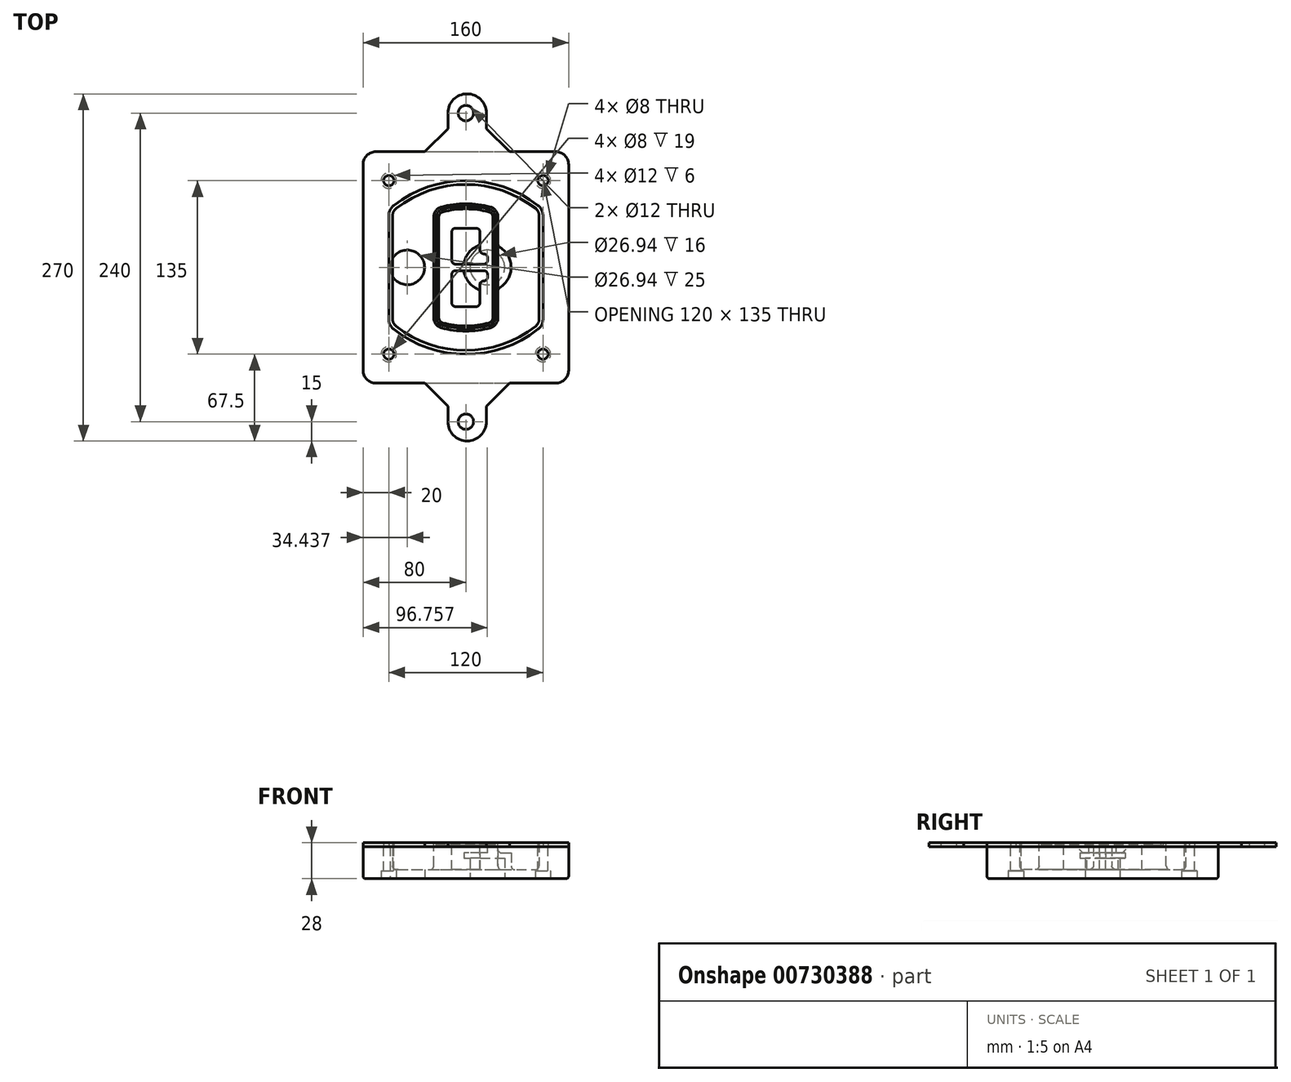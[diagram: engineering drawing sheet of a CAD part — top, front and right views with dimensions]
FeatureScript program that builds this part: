
annotation { "Feature Type Name" : "Feature", "Feature Type Description" : "" }
export const myFeature = defineFeature(function(context is Context, id is Id, definition is map)
    precondition{}
    {
        {
            var Q0;
            Q0=qCreatedBy(makeId("Top.planeOp"),FACE);
            var sketch = newSketch(context, id + "F0", { "sketchPlane" : qUnion([Q0])});
            skPoint(sketch, "E0.rect.middle", {"position": v(0, 0) * mm});
            skLineSegment(sketch, "E1.bottom", {"start": v(-70, -90) * mm, "end": v(70, -90) * mm});
            skLineSegment(sketch, "E1.top", {"start": v(-70, 90) * mm, "end": v(70, 90) * mm});
            skLineSegment(sketch, "E1.left", {"start": v(-80, -80) * mm, "end": v(-80, 80) * mm});
            skLineSegment(sketch, "E1.right", {"start": v(80, -80) * mm, "end": v(80, 80) * mm});
            skLineSegment(sketch, "E2", {"start": v(-80, 90) * mm, "end": v(80, -90) * mm, "construction": true});
            skLineSegment(sketch, "E3", {"start": v(80, 90) * mm, "end": v(-80, -90) * mm, "construction": true});
            skCircle(sketch, "E4", {"center": v(-60, 67.5) * mm, "radius": 4 * mm});
            skCircle(sketch, "E5", {"center": v(60, 67.5) * mm, "radius": 4 * mm});
            skCircle(sketch, "E6", {"center": v(60, -67.5) * mm, "radius": 4 * mm});
            skCircle(sketch, "E7", {"center": v(-60, -67.5) * mm, "radius": 4 * mm});
            skLineSegment(sketch, "E8", {"start": v(-60, 67.5) * mm, "end": v(60, 67.5) * mm, "construction": true});
            skLineSegment(sketch, "E9", {"start": v(60, 67.5) * mm, "end": v(60, -67.5) * mm, "construction": true});
            skLineSegment(sketch, "E10", {"start": v(60, -67.5) * mm, "end": v(-60, -67.5) * mm, "construction": true});
            skLineSegment(sketch, "E11", {"start": v(-60, -67.5) * mm, "end": v(-60, 67.5) * mm, "construction": true});
            skLineSegment(sketch, "E12", {"start": v(-60, 40.3) * mm, "end": v(-60, -40.3) * mm});
            skLineSegment(sketch, "E13", {"start": v(60, 40.3) * mm, "end": v(60, -40.3) * mm});
            skArc(sketch, "E14", {"start": v(56.15, 48.18) * mm, "mid": v(0, 67.5) * mm, "end": v(-56.15, 48.18) * mm});
            skArc(sketch, "E15", {"start": v(-56.15, -48.18) * mm, "mid": v(0, -67.5) * mm, "end": v(56.15, -48.18) * mm});
            skLineSegment(sketch, "E16", {"start": v(-60, 0) * mm, "end": v(60, 0) * mm, "construction": true});
            skPoint(sketch, "E17.visualSharp", {"position": v(-60, -45) * mm});
            skArc(sketch, "E17.filletArc", {"start": v(-60, -40.3) * mm, "mid": v(-58.99, -44.68) * mm, "end": v(-56.15, -48.18) * mm});
            skPoint(sketch, "E18.visualSharp", {"position": v(-60, 45) * mm});
            skArc(sketch, "E18.filletArc", {"start": v(-56.15, 48.18) * mm, "mid": v(-58.99, 44.68) * mm, "end": v(-60, 40.3) * mm});
            skPoint(sketch, "E19.visualSharp", {"position": v(60, 45) * mm});
            skArc(sketch, "E19.filletArc", {"start": v(60, 40.3) * mm, "mid": v(58.99, 44.68) * mm, "end": v(56.15, 48.18) * mm});
            skPoint(sketch, "E20.visualSharp", {"position": v(60, -45) * mm});
            skArc(sketch, "E20.filletArc", {"start": v(56.15, -48.18) * mm, "mid": v(58.99, -44.68) * mm, "end": v(60, -40.3) * mm});
            skPoint(sketch, "E21.visualSharp", {"position": v(-80, 90) * mm});
            skArc(sketch, "E21.filletArc", {"start": v(-70, 90) * mm, "mid": v(-77.07, 87.07) * mm, "end": v(-80, 80) * mm});
            skPoint(sketch, "E22.visualSharp", {"position": v(80, 90) * mm});
            skArc(sketch, "E22.filletArc", {"start": v(80, 80) * mm, "mid": v(77.07, 87.07) * mm, "end": v(70, 90) * mm});
            skPoint(sketch, "E23.visualSharp", {"position": v(80, -90) * mm});
            skArc(sketch, "E23.filletArc", {"start": v(70, -90) * mm, "mid": v(77.07, -87.07) * mm, "end": v(80, -80) * mm});
            skPoint(sketch, "E24.visualSharp", {"position": v(-80, -90) * mm});
            skArc(sketch, "E24.filletArc", {"start": v(-80, -80) * mm, "mid": v(-77.07, -87.07) * mm, "end": v(-70, -90) * mm});
            skArc(sketch, "E25.0", {"start": v(57, 40.3) * mm, "mid": v(56.3, 43.36) * mm, "end": v(54.3, 45.81) * mm});
            skLineSegment(sketch, "E25.1", {"start": v(57, 40.3) * mm, "end": v(57, -40.3) * mm});
            skArc(sketch, "E25.2", {"start": v(54.3, -45.81) * mm, "mid": v(56.3, -43.36) * mm, "end": v(57, -40.3) * mm});
            skArc(sketch, "E25.3", {"start": v(-54.3, -45.81) * mm, "mid": v(0, -64.5) * mm, "end": v(54.3, -45.81) * mm});
            skArc(sketch, "E25.4", {"start": v(-57, -40.3) * mm, "mid": v(-56.3, -43.36) * mm, "end": v(-54.3, -45.81) * mm});
            skArc(sketch, "E25.5", {"start": v(54.3, 45.81) * mm, "mid": v(0, 64.5) * mm, "end": v(-54.3, 45.81) * mm});
            skLineSegment(sketch, "E25.6", {"start": v(-57, 40.3) * mm, "end": v(-57, -40.3) * mm});
            skArc(sketch, "E25.7", {"start": v(-54.3, 45.81) * mm, "mid": v(-56.3, 43.36) * mm, "end": v(-57, 40.3) * mm});
            skArc(sketch, "E26.0", {"start": v(-58.62, 51.33) * mm, "mid": v(-62.58, 46.43) * mm, "end": v(-64, 40.3) * mm});
            skArc(sketch, "E26.1", {"start": v(58.62, 51.33) * mm, "mid": v(0, 71.5) * mm, "end": v(-58.62, 51.33) * mm});
            skArc(sketch, "E26.2", {"start": v(64, 40.3) * mm, "mid": v(62.58, 46.43) * mm, "end": v(58.62, 51.33) * mm});
            skLineSegment(sketch, "E26.3", {"start": v(64, 40.3) * mm, "end": v(64, -40.3) * mm});
            skArc(sketch, "E26.4", {"start": v(58.62, -51.33) * mm, "mid": v(62.58, -46.43) * mm, "end": v(64, -40.3) * mm});
            skLineSegment(sketch, "E26.5", {"start": v(-64, 40.3) * mm, "end": v(-64, -40.3) * mm});
            skArc(sketch, "E26.6", {"start": v(-58.62, -51.33) * mm, "mid": v(0, -71.5) * mm, "end": v(58.62, -51.33) * mm});
            skArc(sketch, "E26.7", {"start": v(-64, -40.3) * mm, "mid": v(-62.58, -46.43) * mm, "end": v(-58.62, -51.33) * mm});
            skSolve(sketch);
        }
        {
            var Q0;
            Q0=makeQuery(id+"F0.imprint","IMPRINT",FACE,{"disambiguationData":[TD([[makeQuery(id+"F0.imprint","IMPRINT",EDGE,{"derivedFrom":sQuery(id+"F0.wireOp",EDGE,"E1.bottom")}),1.0]])]});
            var Q1;
            Q1=makeQuery(id+"F0.imprint","IMPRINT",FACE,{"disambiguationData":[TD([[makeQuery(id+"F0.imprint","IMPRINT",EDGE,{"derivedFrom":sQuery(id+"F0.wireOp",EDGE,"E12")}),1.0]])]});
            var Q2;
            Q2=makeQuery(id+"F0.imprint","IMPRINT",FACE,{"disambiguationData":[TD([[makeQuery(id+"F0.imprint","IMPRINT",EDGE,{"derivedFrom":sQuery(id+"F0.wireOp",EDGE,"E25.0")}),1.0]])]});
            var Q3;
            Q3=makeQuery(id+"F0.imprint","IMPRINT",FACE,{"disambiguationData":[TD([[makeQuery(id+"F0.imprint","IMPRINT",EDGE,{"derivedFrom":sQuery(id+"F0.wireOp",EDGE,"E12")}),-1.0]])]});
            extrude(context, id + "F1", {"entities" : qUnion([Q0, Q1, Q2, Q3]), "oppositeDirection" : true, "depth" : 25 * mm});
        }
        {
            var Q0;
            Q0=makeQuery(id+"F0.imprint","IMPRINT",FACE,{"disambiguationData":[TD([[makeQuery(id+"F0.imprint","IMPRINT",EDGE,{"derivedFrom":sQuery(id+"F0.wireOp",EDGE,"E12")}),1.0]])]});
            extrude(context, id + "F2", {"entities" : qUnion([Q0]), "operationType" : NewBodyOperationType.ADD, "depth" : 3 * mm});
        }
        {
            var Q0;
            Q0=makeQuery(id+"F0.imprint","IMPRINT",FACE,{"disambiguationData":[TD([[makeQuery(id+"F0.imprint","IMPRINT",EDGE,{"derivedFrom":sQuery(id+"F0.wireOp",EDGE,"E25.0")}),1.0]])]});
            extrude(context, id + "F3", {"entities" : qUnion([Q0]), "operationType" : NewBodyOperationType.REMOVE, "oppositeDirection" : true, "depth" : 18 * mm});
        }
        {
            var Q0;
            Q0=makeQuery(id+"F2.opExtrude","CAP_FACE",FACE,{"disambiguationData":[OSD([sQuery(id+"F0.wireOp",EDGE,"E12"),sQuery(id+"F0.wireOp",EDGE,"E13"),sQuery(id+"F0.wireOp",EDGE,"E14"),sQuery(id+"F0.wireOp",EDGE,"E15"),sQuery(id+"F0.wireOp",EDGE,"E17.filletArc"),sQuery(id+"F0.wireOp",EDGE,"E18.filletArc"),sQuery(id+"F0.wireOp",EDGE,"E19.filletArc"),sQuery(id+"F0.wireOp",EDGE,"E20.filletArc"),sQuery(id+"F0.wireOp",EDGE,"E25.0"),sQuery(id+"F0.wireOp",EDGE,"E25.1"),sQuery(id+"F0.wireOp",EDGE,"E25.2"),sQuery(id+"F0.wireOp",EDGE,"E25.3"),sQuery(id+"F0.wireOp",EDGE,"E25.4"),sQuery(id+"F0.wireOp",EDGE,"E25.5"),sQuery(id+"F0.wireOp",EDGE,"E25.6"),sQuery(id+"F0.wireOp",EDGE,"E25.7")])],"isStart":false});
            var sketch = newSketch(context, id + "F4", { "sketchPlane" : qUnion([Q0])});
            skArc(sketch, "E27.0", {"start": v(-19.08, -46.97) * mm, "mid": v(0, -49.5) * mm, "end": v(19.08, -46.97) * mm});
            skArc(sketch, "E28.0", {"start": v(19.08, 46.97) * mm, "mid": v(0, 49.5) * mm, "end": v(-19.08, 46.97) * mm});
            skLineSegment(sketch, "E29", {"start": v(-25, 39.25) * mm, "end": v(-25, -39.25) * mm});
            skLineSegment(sketch, "E30", {"start": v(25, 39.25) * mm, "end": v(25, -39.25) * mm});
            skLineSegment(sketch, "E31", {"start": v(-25, 45.1) * mm, "end": v(25, 45.1) * mm, "construction": true});
            skLineSegment(sketch, "E32", {"start": v(-25, -45.1) * mm, "end": v(25, -45.1) * mm, "construction": true});
            skPoint(sketch, "E33.visualSharp", {"position": v(-25, 45.1) * mm});
            skArc(sketch, "E33.filletArc", {"start": v(-19.08, 46.97) * mm, "mid": v(-23.35, 44.11) * mm, "end": v(-25, 39.25) * mm});
            skPoint(sketch, "E34.visualSharp", {"position": v(25, 45.1) * mm});
            skArc(sketch, "E34.filletArc", {"start": v(25, 39.25) * mm, "mid": v(23.35, 44.11) * mm, "end": v(19.08, 46.97) * mm});
            skPoint(sketch, "E35.visualSharp", {"position": v(25, -45.1) * mm});
            skArc(sketch, "E35.filletArc", {"start": v(19.08, -46.97) * mm, "mid": v(23.35, -44.11) * mm, "end": v(25, -39.25) * mm});
            skPoint(sketch, "E36.visualSharp", {"position": v(-25, -45.1) * mm});
            skArc(sketch, "E36.filletArc", {"start": v(-25, -39.25) * mm, "mid": v(-23.35, -44.11) * mm, "end": v(-19.08, -46.97) * mm});
            skArc(sketch, "E37.0", {"start": v(54.3, 45.81) * mm, "mid": v(0, 64.5) * mm, "end": v(-54.3, 45.81) * mm});
            skArc(sketch, "E37.1", {"start": v(-54.3, 45.81) * mm, "mid": v(-56.3, 43.36) * mm, "end": v(-57, 40.3) * mm});
            skLineSegment(sketch, "E37.2", {"start": v(-57, 40.3) * mm, "end": v(-57, -40.3) * mm});
            skArc(sketch, "E37.3", {"start": v(-57, -40.3) * mm, "mid": v(-56.3, -43.36) * mm, "end": v(-54.3, -45.81) * mm});
            skArc(sketch, "E37.4", {"start": v(-54.3, -45.81) * mm, "mid": v(0, -64.5) * mm, "end": v(54.3, -45.81) * mm});
            skArc(sketch, "E37.5", {"start": v(54.3, -45.81) * mm, "mid": v(56.3, -43.36) * mm, "end": v(57, -40.3) * mm});
            skLineSegment(sketch, "E37.6", {"start": v(57, 40.3) * mm, "end": v(57, -40.3) * mm});
            skArc(sketch, "E37.7", {"start": v(57, 40.3) * mm, "mid": v(56.3, 43.36) * mm, "end": v(54.3, 45.81) * mm});
            skLineSegment(sketch, "E38.0", {"start": v(23, 39.25) * mm, "end": v(23, -39.25) * mm});
            skArc(sketch, "E38.1", {"start": v(18.56, -45.04) * mm, "mid": v(21.76, -42.9) * mm, "end": v(23, -39.25) * mm});
            skArc(sketch, "E38.2", {"start": v(-18.56, -45.04) * mm, "mid": v(0, -47.5) * mm, "end": v(18.56, -45.04) * mm});
            skArc(sketch, "E38.3", {"start": v(-23, -39.25) * mm, "mid": v(-21.76, -42.9) * mm, "end": v(-18.56, -45.04) * mm});
            skLineSegment(sketch, "E38.4", {"start": v(-23, 39.25) * mm, "end": v(-23, -39.25) * mm});
            skArc(sketch, "E38.5", {"start": v(23, 39.25) * mm, "mid": v(21.76, 42.9) * mm, "end": v(18.56, 45.04) * mm});
            skArc(sketch, "E38.6", {"start": v(-18.56, 45.04) * mm, "mid": v(-21.76, 42.9) * mm, "end": v(-23, 39.25) * mm});
            skArc(sketch, "E38.7", {"start": v(18.56, 45.04) * mm, "mid": v(0, 47.5) * mm, "end": v(-18.56, 45.04) * mm});
            skArc(sketch, "E39.0", {"start": v(21, 39.25) * mm, "mid": v(20.18, 41.68) * mm, "end": v(18.04, 43.1) * mm});
            skLineSegment(sketch, "E39.1", {"start": v(21, 39.25) * mm, "end": v(21, -39.25) * mm});
            skArc(sketch, "E39.2", {"start": v(18.04, -43.1) * mm, "mid": v(20.18, -41.68) * mm, "end": v(21, -39.25) * mm});
            skArc(sketch, "E39.3", {"start": v(-18.04, -43.1) * mm, "mid": v(0, -45.5) * mm, "end": v(18.04, -43.1) * mm});
            skArc(sketch, "E39.4", {"start": v(-21, -39.25) * mm, "mid": v(-20.18, -41.68) * mm, "end": v(-18.04, -43.1) * mm});
            skArc(sketch, "E39.5", {"start": v(18.04, 43.1) * mm, "mid": v(0, 45.5) * mm, "end": v(-18.04, 43.1) * mm});
            skLineSegment(sketch, "E39.6", {"start": v(-21, 39.25) * mm, "end": v(-21, -39.25) * mm});
            skArc(sketch, "E39.7", {"start": v(-18.04, 43.1) * mm, "mid": v(-20.18, 41.68) * mm, "end": v(-21, 39.25) * mm});
            skLineSegment(sketch, "E40", {"start": v(-25, 0) * mm, "end": v(25, 0) * mm, "construction": true});
            skLineSegment(sketch, "E41", {"start": v(-11, 5.5) * mm, "end": v(-11, 27.5) * mm});
            skLineSegment(sketch, "E42", {"start": v(-8, 30.5) * mm, "end": v(8, 30.5) * mm});
            skLineSegment(sketch, "E43", {"start": v(11, 27.5) * mm, "end": v(11, 13.5) * mm});
            skLineSegment(sketch, "E44", {"start": v(14, 10.5) * mm, "end": v(14, 10.5) * mm});
            skLineSegment(sketch, "E45", {"start": v(17, 7.5) * mm, "end": v(17, 5.5) * mm});
            skLineSegment(sketch, "E46", {"start": v(14, 2.5) * mm, "end": v(-8, 2.5) * mm});
            skPoint(sketch, "E47.visualSharp", {"position": v(-11, 30.5) * mm});
            skArc(sketch, "E47.filletArc", {"start": v(-8, 30.5) * mm, "mid": v(-10.12, 29.62) * mm, "end": v(-11, 27.5) * mm});
            skPoint(sketch, "E48.visualSharp", {"position": v(11, 30.5) * mm});
            skArc(sketch, "E48.filletArc", {"start": v(11, 27.5) * mm, "mid": v(10.12, 29.62) * mm, "end": v(8, 30.5) * mm});
            skPoint(sketch, "E49.visualSharp", {"position": v(11, 10.5) * mm});
            skArc(sketch, "E49.filletArc", {"start": v(11, 13.5) * mm, "mid": v(11.88, 11.38) * mm, "end": v(14, 10.5) * mm});
            skPoint(sketch, "E50.visualSharp", {"position": v(17, 10.5) * mm});
            skArc(sketch, "E50.filletArc", {"start": v(17, 7.5) * mm, "mid": v(16.12, 9.62) * mm, "end": v(14, 10.5) * mm});
            skPoint(sketch, "E51.visualSharp", {"position": v(17, 2.5) * mm});
            skArc(sketch, "E51.filletArc", {"start": v(14, 2.5) * mm, "mid": v(16.12, 3.38) * mm, "end": v(17, 5.5) * mm});
            skPoint(sketch, "E52.visualSharp", {"position": v(-11, 2.5) * mm});
            skArc(sketch, "E52.filletArc", {"start": v(-11, 5.5) * mm, "mid": v(-10.12, 3.38) * mm, "end": v(-8, 2.5) * mm});
            skLineSegment(sketch, "E53.0.MirrorCS", {"start": v(14, -2.5) * mm, "end": v(-8, -2.5) * mm});
            skArc(sketch, "E54.0.MirrorCS", {"start": v(-11, -5.5) * mm, "mid": v(-10.12, -3.38) * mm, "end": v(-8, -2.5) * mm});
            skLineSegment(sketch, "E55.0.MirrorCS", {"start": v(-11, -5.5) * mm, "end": v(-11, -27.5) * mm});
            skArc(sketch, "E56.0.MirrorCS", {"start": v(-8, -30.5) * mm, "mid": v(-10.12, -29.62) * mm, "end": v(-11, -27.5) * mm});
            skLineSegment(sketch, "E57.0.MirrorCS", {"start": v(-8, -30.5) * mm, "end": v(8, -30.5) * mm});
            skArc(sketch, "E58.0.MirrorCS", {"start": v(11, -27.5) * mm, "mid": v(10.12, -29.62) * mm, "end": v(8, -30.5) * mm});
            skLineSegment(sketch, "E59.0.MirrorCS", {"start": v(11, -27.5) * mm, "end": v(11, -13.5) * mm});
            skArc(sketch, "E60.0.MirrorCS", {"start": v(11, -13.5) * mm, "mid": v(11.88, -11.38) * mm, "end": v(14, -10.5) * mm});
            skArc(sketch, "E61.0.MirrorCS", {"start": v(17, -7.5) * mm, "mid": v(16.12, -9.62) * mm, "end": v(14, -10.5) * mm});
            skLineSegment(sketch, "E62.0.MirrorCS", {"start": v(17, -7.5) * mm, "end": v(17, -5.5) * mm});
            skArc(sketch, "E63.0.MirrorCS", {"start": v(14, -2.5) * mm, "mid": v(16.12, -3.38) * mm, "end": v(17, -5.5) * mm});
            skSolve(sketch);
        }
        {
            var Q0;
            Q0=makeQuery(id+"F4.imprint","IMPRINT",FACE,{"disambiguationData":[TD([[makeQuery(id+"F4.imprint","IMPRINT",EDGE,{"derivedFrom":sQuery(id+"F4.wireOp",EDGE,"E27.0")}),1.0]])]});
            var Q1;
            Q1=makeQuery(id+"F4.imprint","IMPRINT",FACE,{"disambiguationData":[TD([[makeQuery(id+"F4.imprint","IMPRINT",EDGE,{"derivedFrom":sQuery(id+"F4.wireOp",EDGE,"E38.0")}),-1.0]])]});
            var Q2;
            Q2=makeQuery(id+"F4.imprint","IMPRINT",FACE,{"disambiguationData":[TD([[makeQuery(id+"F4.imprint","IMPRINT",EDGE,{"derivedFrom":sQuery(id+"F4.wireOp",EDGE,"E39.0")}),1.0]])]});
            extrude(context, id + "F5", {"entities" : qUnion([Q0, Q1, Q2]), "operationType" : NewBodyOperationType.ADD, "endBound" : BoundingType.UP_TO_NEXT, "oppositeDirection" : true, "depth" : 25 * mm});
        }
        {
            var Q0;
            Q0=makeQuery(id+"F4.imprint","IMPRINT",FACE,{"disambiguationData":[TD([[makeQuery(id+"F4.imprint","IMPRINT",EDGE,{"derivedFrom":sQuery(id+"F4.wireOp",EDGE,"E38.0")}),-1.0]])]});
            extrude(context, id + "F6", {"entities" : qUnion([Q0]), "operationType" : NewBodyOperationType.REMOVE, "oppositeDirection" : true, "depth" : 2 * mm});
        }
        {
            var Q0;
            Q0=makeQuery(id+"F1.opExtrude","CAP_FACE",FACE,{"disambiguationData":[OSD([sQuery(id+"F0.wireOp",EDGE,"E1.bottom"),sQuery(id+"F0.wireOp",EDGE,"E1.top"),sQuery(id+"F0.wireOp",EDGE,"E1.left"),sQuery(id+"F0.wireOp",EDGE,"E1.right"),sQuery(id+"F0.wireOp",EDGE,"E4"),sQuery(id+"F0.wireOp",EDGE,"E5"),sQuery(id+"F0.wireOp",EDGE,"E6"),sQuery(id+"F0.wireOp",EDGE,"E7"),sQuery(id+"F0.wireOp",EDGE,"E21.filletArc"),sQuery(id+"F0.wireOp",EDGE,"E22.filletArc"),sQuery(id+"F0.wireOp",EDGE,"E23.filletArc"),sQuery(id+"F0.wireOp",EDGE,"E24.filletArc")])],"isStart":false});
            var sketch = newSketch(context, id + "F7", { "sketchPlane" : qUnion([Q0])});
            skCircle(sketch, "E64", {"center": v(16.76, 0) * mm, "radius": 13.47 * mm});
            skCircle(sketch, "E65", {"center": v(-45.56, 0) * mm, "radius": 13.47 * mm});
            skLineSegment(sketch, "E66", {"start": v(80, 0) * mm, "end": v(-80, 0) * mm});
            skCircle(sketch, "E67", {"center": v(16.76, 0) * mm, "radius": 18.47 * mm});
            skCircle(sketch, "E68", {"center": v(60, -67.5) * mm, "radius": 6 * mm});
            skCircle(sketch, "E69", {"center": v(-60, -67.5) * mm, "radius": 6 * mm});
            skCircle(sketch, "E70", {"center": v(-60, 67.5) * mm, "radius": 6 * mm});
            skCircle(sketch, "E71", {"center": v(60, 67.5) * mm, "radius": 6 * mm});
            skSolve(sketch);
        }
        {
            var Q0;
            {var subQ1=sQuery(id+"F7.wireOp",EDGE,"E66");var subQ4=sQuery(id+"F7.wireOp",EDGE,"E64");var subQ6=makeQuery(id+"F7.imprint","INTERSECT",VERTEX,{"disambiguationData":[OD(0.0)],"derivedFrom":[subQ4,subQ1]});Q0=makeQuery(id+"F7.imprint","IMPRINT",FACE,{"disambiguationData":[TD([[makeQuery(id+"F7.imprint","IMPRINT",EDGE,{"disambiguationData":[TD([[subQ6,-1.0]])],"derivedFrom":subQ4}),-1.0]])]});}
            var Q1;
            {var subQ0=sQuery(id+"F7.wireOp",EDGE,"E66");var subQ1=sQuery(id+"F7.wireOp",EDGE,"E64");var subQ3=makeQuery(id+"F7.imprint","INTERSECT",VERTEX,{"disambiguationData":[OD(0.0)],"derivedFrom":[subQ1,subQ0]});Q1=makeQuery(id+"F7.imprint","IMPRINT",FACE,{"disambiguationData":[TD([[makeQuery(id+"F7.imprint","IMPRINT",EDGE,{"disambiguationData":[TD([[subQ3,-1.0]])],"derivedFrom":subQ1}),1.0]])]});}
            var Q2;
            {var subQ0=sQuery(id+"F7.wireOp",EDGE,"E66");var subQ1=sQuery(id+"F7.wireOp",EDGE,"E64");var subQ3=makeQuery(id+"F7.imprint","INTERSECT",VERTEX,{"disambiguationData":[OD(0.0)],"derivedFrom":[subQ1,subQ0]});Q2=makeQuery(id+"F7.imprint","IMPRINT",FACE,{"disambiguationData":[TD([[makeQuery(id+"F7.imprint","IMPRINT",EDGE,{"disambiguationData":[TD([[subQ3,1.0]])],"derivedFrom":subQ1}),1.0]])]});}
            var Q3;
            {var subQ1=sQuery(id+"F7.wireOp",EDGE,"E66");var subQ4=sQuery(id+"F7.wireOp",EDGE,"E64");var subQ6=makeQuery(id+"F7.imprint","INTERSECT",VERTEX,{"disambiguationData":[OD(0.0)],"derivedFrom":[subQ4,subQ1]});Q3=makeQuery(id+"F7.imprint","IMPRINT",FACE,{"disambiguationData":[TD([[makeQuery(id+"F7.imprint","IMPRINT",EDGE,{"disambiguationData":[TD([[subQ6,1.0]])],"derivedFrom":subQ4}),-1.0]])]});}
            extrude(context, id + "F8", {"entities" : qUnion([Q0, Q1, Q2, Q3]), "operationType" : NewBodyOperationType.ADD, "oppositeDirection" : true, "depth" : 20 * mm});
        }
        {
            var Q0;
            {var subQ0=sQuery(id+"F7.wireOp",EDGE,"E66");var subQ1=sQuery(id+"F7.wireOp",EDGE,"E64");var subQ3=makeQuery(id+"F7.imprint","INTERSECT",VERTEX,{"disambiguationData":[OD(0.0)],"derivedFrom":[subQ1,subQ0]});Q0=makeQuery(id+"F7.imprint","IMPRINT",FACE,{"disambiguationData":[TD([[makeQuery(id+"F7.imprint","IMPRINT",EDGE,{"disambiguationData":[TD([[subQ3,-1.0]])],"derivedFrom":subQ1}),1.0]])]});}
            var Q1;
            {var subQ0=sQuery(id+"F7.wireOp",EDGE,"E66");var subQ1=sQuery(id+"F7.wireOp",EDGE,"E64");var subQ3=makeQuery(id+"F7.imprint","INTERSECT",VERTEX,{"disambiguationData":[OD(0.0)],"derivedFrom":[subQ1,subQ0]});Q1=makeQuery(id+"F7.imprint","IMPRINT",FACE,{"disambiguationData":[TD([[makeQuery(id+"F7.imprint","IMPRINT",EDGE,{"disambiguationData":[TD([[subQ3,1.0]])],"derivedFrom":subQ1}),1.0]])]});}
            extrude(context, id + "F9", {"entities" : qUnion([Q0, Q1]), "operationType" : NewBodyOperationType.REMOVE, "oppositeDirection" : true, "depth" : 16 * mm});
        }
        {
            var Q0;
            {var subQ0=sQuery(id+"F7.wireOp",EDGE,"E66");var subQ1=sQuery(id+"F7.wireOp",EDGE,"E65");var subQ3=makeQuery(id+"F7.imprint","INTERSECT",VERTEX,{"disambiguationData":[OD(0.0)],"derivedFrom":[subQ1,subQ0]});Q0=makeQuery(id+"F7.imprint","IMPRINT",FACE,{"disambiguationData":[TD([[makeQuery(id+"F7.imprint","IMPRINT",EDGE,{"disambiguationData":[TD([[subQ3,-1.0]])],"derivedFrom":subQ1}),1.0]])]});}
            var Q1;
            {var subQ0=sQuery(id+"F7.wireOp",EDGE,"E66");var subQ1=sQuery(id+"F7.wireOp",EDGE,"E65");var subQ3=makeQuery(id+"F7.imprint","INTERSECT",VERTEX,{"disambiguationData":[OD(0.0)],"derivedFrom":[subQ1,subQ0]});Q1=makeQuery(id+"F7.imprint","IMPRINT",FACE,{"disambiguationData":[TD([[makeQuery(id+"F7.imprint","IMPRINT",EDGE,{"disambiguationData":[TD([[subQ3,1.0]])],"derivedFrom":subQ1}),1.0]])]});}
            extrude(context, id + "F10", {"entities" : qUnion([Q0, Q1]), "operationType" : NewBodyOperationType.REMOVE, "oppositeDirection" : true, "depth" : 25 * mm});
        }
        {
            var Q0;
            Q0=makeQuery(id+"F7.imprint","IMPRINT",FACE,{"disambiguationData":[TD([[makeQuery(id+"F7.imprint","IMPRINT",EDGE,{"derivedFrom":sQuery(id+"F7.wireOp",EDGE,"E68")}),1.0]])]});
            var Q1;
            Q1=makeQuery(id+"F7.imprint","IMPRINT",FACE,{"disambiguationData":[TD([[makeQuery(id+"F7.imprint","IMPRINT",EDGE,{"derivedFrom":makeQuery(id+"F1.opExtrude","CAP_EDGE",EDGE,{"disambiguationData":[OSD([sQuery(id+"F0.wireOp",EDGE,"E5")])],"isStart":false})}),-1.0]])]});
            var Q2;
            Q2=makeQuery(id+"F7.imprint","IMPRINT",FACE,{"disambiguationData":[TD([[makeQuery(id+"F7.imprint","IMPRINT",EDGE,{"derivedFrom":sQuery(id+"F7.wireOp",EDGE,"E69")}),1.0]])]});
            var Q3;
            Q3=makeQuery(id+"F7.imprint","IMPRINT",FACE,{"disambiguationData":[TD([[makeQuery(id+"F7.imprint","IMPRINT",EDGE,{"derivedFrom":makeQuery(id+"F1.opExtrude","CAP_EDGE",EDGE,{"disambiguationData":[OSD([sQuery(id+"F0.wireOp",EDGE,"E4")])],"isStart":false})}),-1.0]])]});
            var Q4;
            Q4=makeQuery(id+"F7.imprint","IMPRINT",FACE,{"disambiguationData":[TD([[makeQuery(id+"F7.imprint","IMPRINT",EDGE,{"derivedFrom":sQuery(id+"F7.wireOp",EDGE,"E70")}),1.0]])]});
            var Q5;
            Q5=makeQuery(id+"F7.imprint","IMPRINT",FACE,{"disambiguationData":[TD([[makeQuery(id+"F7.imprint","IMPRINT",EDGE,{"derivedFrom":makeQuery(id+"F1.opExtrude","CAP_EDGE",EDGE,{"disambiguationData":[OSD([sQuery(id+"F0.wireOp",EDGE,"E7")])],"isStart":false})}),-1.0]])]});
            var Q6;
            Q6=makeQuery(id+"F7.imprint","IMPRINT",FACE,{"disambiguationData":[TD([[makeQuery(id+"F7.imprint","IMPRINT",EDGE,{"derivedFrom":sQuery(id+"F7.wireOp",EDGE,"E71")}),1.0]])]});
            var Q7;
            Q7=makeQuery(id+"F7.imprint","IMPRINT",FACE,{"disambiguationData":[TD([[makeQuery(id+"F7.imprint","IMPRINT",EDGE,{"derivedFrom":makeQuery(id+"F1.opExtrude","CAP_EDGE",EDGE,{"disambiguationData":[OSD([sQuery(id+"F0.wireOp",EDGE,"E6")])],"isStart":false})}),-1.0]])]});
            extrude(context, id + "F11", {"entities" : qUnion([Q0, Q1, Q2, Q3, Q4, Q5, Q6, Q7]), "operationType" : NewBodyOperationType.REMOVE, "oppositeDirection" : true, "depth" : 6 * mm});
        }
        {
            var Q0;
            Q0=makeQuery(id+"F9.boolean.opBoolean","COPY",FACE,{"derivedFrom":makeQuery(id+"F9.opExtrude","CAP_FACE",FACE,{"disambiguationData":[OSD([sQuery(id+"F7.wireOp",EDGE,"E64")])],"isStart":false})});
            var sketch = newSketch(context, id + "F12", { "sketchPlane" : qUnion([Q0])});
            skArc(sketch, "E72.0", {"start": v(11, 17.55) * mm, "mid": v(2.57, 11.82) * mm, "end": v(-1.54, 2.5) * mm});
            skArc(sketch, "E72.1", {"start": v(-1.54, -2.5) * mm, "mid": v(2.57, -11.82) * mm, "end": v(11, -17.55) * mm});
            skLineSegment(sketch, "E73", {"start": v(-1.54, -2.5) * mm, "end": v(14, -2.5) * mm});
            skLineSegment(sketch, "E74.0", {"start": v(14, 2.5) * mm, "end": v(-1.54, 2.5) * mm});
            skArc(sketch, "E74.1", {"start": v(14, 2.5) * mm, "mid": v(16.12, 3.38) * mm, "end": v(17, 5.5) * mm});
            skLineSegment(sketch, "E74.2", {"start": v(17, 7.5) * mm, "end": v(17, 5.5) * mm});
            skArc(sketch, "E74.3", {"start": v(17, 7.5) * mm, "mid": v(16.12, 9.62) * mm, "end": v(14, 10.5) * mm});
            skArc(sketch, "E74.4", {"start": v(11, 13.5) * mm, "mid": v(11.88, 11.38) * mm, "end": v(14, 10.5) * mm});
            skLineSegment(sketch, "E74.5", {"start": v(11, 17.55) * mm, "end": v(11, 13.5) * mm});
            skLineSegment(sketch, "E74.7", {"start": v(14, -2.5) * mm, "end": v(-1.54, -2.5) * mm});
            skArc(sketch, "E74.8", {"start": v(14, -2.5) * mm, "mid": v(16.12, -3.38) * mm, "end": v(17, -5.5) * mm});
            skLineSegment(sketch, "E74.9", {"start": v(17, -7.5) * mm, "end": v(17, -5.5) * mm});
            skArc(sketch, "E74.10", {"start": v(17, -7.5) * mm, "mid": v(16.12, -9.62) * mm, "end": v(14, -10.5) * mm});
            skArc(sketch, "E74.11", {"start": v(11, -13.5) * mm, "mid": v(11.88, -11.38) * mm, "end": v(14, -10.5) * mm});
            skLineSegment(sketch, "E74.12", {"start": v(11, -17.55) * mm, "end": v(11, -13.5) * mm});
            skPoint(sketch, "E75.orphan", {"position": v(11, -27.5) * mm});
            skPoint(sketch, "E76.orphan", {"position": v(-8, -2.5) * mm});
            skPoint(sketch, "E77.orphan", {"position": v(-8, 2.5) * mm});
            skPoint(sketch, "E78.orphan", {"position": v(11, 27.5) * mm});
            skSolve(sketch);
        }
        {
            var Q0;
            {var subQ7=sQuery(id+"F12.wireOp",EDGE,"E72.0");var subQ14=sQuery(id+"F12.wireOp",EDGE,"E72.1");var subQ16=sQuery(id+"F12.wireOp",EDGE,"E74.1");var subQ18=sQuery(id+"F12.wireOp",EDGE,"E74.8");Q0=qUnion([makeQuery(id+"F12.imprint","IMPRINT",FACE,{"disambiguationData":[TD([[makeQuery(id+"F12.imprint","IMPRINT",EDGE,{"derivedFrom":subQ7}),1.0]])]}),makeQuery(id+"F12.imprint","IMPRINT",FACE,{"disambiguationData":[TD([[makeQuery(id+"F12.imprint","IMPRINT",EDGE,{"derivedFrom":subQ14}),1.0]])]}),makeQuery(id+"F12.imprint","IMPRINT",FACE,{"disambiguationData":[TD([[makeQuery(id+"F12.imprint","IMPRINT",EDGE,{"derivedFrom":subQ16}),1.0]])]}),makeQuery(id+"F12.imprint","IMPRINT",FACE,{"disambiguationData":[TD([[makeQuery(id+"F12.imprint","IMPRINT",EDGE,{"derivedFrom":subQ18}),-1.0]])]})]);}
            var Q1;
            Q1=makeQuery(id+"F5.boolean.opBoolean","SPLIT",FACE,{"disambiguationData":[TD([makeQuery(id+"F5.opExtrude","SWEPT_FACE",FACE,{"disambiguationData":[OSD([sQuery(id+"F4.wireOp",EDGE,"E41")])]})])],"derivedFrom":makeQuery(id+"F3.boolean.opBoolean","COPY",FACE,{"derivedFrom":makeQuery(id+"F3.opExtrude","CAP_FACE",FACE,{"disambiguationData":[OSD([sQuery(id+"F0.wireOp",EDGE,"E25.0"),sQuery(id+"F0.wireOp",EDGE,"E25.1"),sQuery(id+"F0.wireOp",EDGE,"E25.2"),sQuery(id+"F0.wireOp",EDGE,"E25.3"),sQuery(id+"F0.wireOp",EDGE,"E25.4"),sQuery(id+"F0.wireOp",EDGE,"E25.5"),sQuery(id+"F0.wireOp",EDGE,"E25.6"),sQuery(id+"F0.wireOp",EDGE,"E25.7")])],"isStart":false})})});
            extrude(context, id + "F13", {"entities" : qUnion([Q0]), "operationType" : NewBodyOperationType.REMOVE, "endBound" : BoundingType.UP_TO_SURFACE, "endBoundEntityFace" : qUnion([Q1]), "depth" : 25 * mm});
        }
        {
            var Q0;
            Q0=makeQuery(id+"F3.boolean.opBoolean","COPY",EDGE,{"derivedFrom":makeQuery(id+"F3.opExtrude","CAP_EDGE",EDGE,{"disambiguationData":[OSD([sQuery(id+"F0.wireOp",EDGE,"E25.6")])],"isStart":false})});
            var Q1;
            Q1=makeQuery(id+"F8.boolean.opBoolean","INTERSECT",EDGE,{"derivedFrom":[makeQuery(id+"F5.opExtrude","SWEPT_FACE",FACE,{"disambiguationData":[OSD([sQuery(id+"F4.wireOp",EDGE,"E30")])]}),makeQuery(id+"F8.opExtrude","CAP_FACE",FACE,{"disambiguationData":[OSD([sQuery(id+"F7.wireOp",EDGE,"E67")])],"isStart":false})]});
            var Q2;
            Q2=makeQuery(id+"F8.boolean.opBoolean","INTERSECT",EDGE,{"disambiguationData":[OD(1.0)],"derivedFrom":[makeQuery(id+"F5.opExtrude","SWEPT_FACE",FACE,{"disambiguationData":[OSD([sQuery(id+"F4.wireOp",EDGE,"E30")])]}),makeQuery(id+"F8.opExtrude","SWEPT_FACE",FACE,{"disambiguationData":[OSD([sQuery(id+"F7.wireOp",EDGE,"E67")])]})]});
            var Q3;
            {var subQ0=sQuery(id+"F4.wireOp",EDGE,"E30");Q3=makeQuery(id+"F8.boolean.opBoolean","SPLIT",EDGE,{"disambiguationData":[TD([makeQuery(id+"F5.opExtrude","SWEPT_FACE",FACE,{"disambiguationData":[OSD([sQuery(id+"F4.wireOp",EDGE,"E35.filletArc")])]})])],"derivedFrom":makeQuery(id+"F5.opExtrude","CAP_EDGE",EDGE,{"disambiguationData":[OSD([subQ0])],"isStart":false})});}
            var Q4;
            {var subQ0=sQuery(id+"F0.wireOp",EDGE,"E25.7");var subQ1=sQuery(id+"F0.wireOp",EDGE,"E25.1");var subQ2=sQuery(id+"F0.wireOp",EDGE,"E25.6");var subQ3=sQuery(id+"F0.wireOp",EDGE,"E25.5");var subQ4=sQuery(id+"F0.wireOp",EDGE,"E25.4");var subQ5=sQuery(id+"F0.wireOp",EDGE,"E25.0");var subQ6=sQuery(id+"F0.wireOp",EDGE,"E25.2");var subQ7=sQuery(id+"F0.wireOp",EDGE,"E25.3");Q4=makeQuery(id+"F8.boolean.opBoolean","INTERSECT",EDGE,{"derivedFrom":[makeQuery(id+"F5.boolean.opBoolean","SPLIT",FACE,{"disambiguationData":[TD([makeQuery(id+"F2.opExtrude","SWEPT_FACE",FACE,{"disambiguationData":[OSD([subQ5])]})])],"derivedFrom":makeQuery(id+"F3.boolean.opBoolean","COPY",FACE,{"derivedFrom":makeQuery(id+"F3.opExtrude","CAP_FACE",FACE,{"disambiguationData":[OSD([subQ5,subQ1,subQ6,subQ7,subQ4,subQ3,subQ2,subQ0])],"isStart":false})})}),makeQuery(id+"F8.opExtrude","SWEPT_FACE",FACE,{"disambiguationData":[OSD([sQuery(id+"F7.wireOp",EDGE,"E67")])]})]});}
            var Q5;
            Q5=makeQuery(id+"F8.boolean.opBoolean","INTERSECT",EDGE,{"disambiguationData":[OD(0.0)],"derivedFrom":[makeQuery(id+"F5.opExtrude","SWEPT_FACE",FACE,{"disambiguationData":[OSD([sQuery(id+"F4.wireOp",EDGE,"E30")])]}),makeQuery(id+"F8.opExtrude","SWEPT_FACE",FACE,{"disambiguationData":[OSD([sQuery(id+"F7.wireOp",EDGE,"E67")])]})]});
            fillet(context, id + "F14", {"entities" : qUnion([Q0, Q1, Q2, Q3, Q4, Q5]), "radius" : 3 * mm, "tangentPropagation" : true, "allowEdgeOverflow" : false});
        }
        {
            var Q0;
            Q0=makeQuery(id+"F1.opExtrude","CAP_EDGE",EDGE,{"disambiguationData":[OSD([sQuery(id+"F0.wireOp",EDGE,"E1.bottom")])],"isStart":false});
            fillet(context, id + "F15", {"entities" : qUnion([Q0]), "radius" : 2 * mm, "tangentPropagation" : true, "allowEdgeOverflow" : false});
        }
        {
            var Q0;
            {var subQ0=sQuery(id+"F0.wireOp",EDGE,"E21.filletArc");var subQ1=sQuery(id+"F0.wireOp",EDGE,"E7");var subQ2=sQuery(id+"F0.wireOp",EDGE,"E6");var subQ3=sQuery(id+"F0.wireOp",EDGE,"E5");var subQ4=sQuery(id+"F0.wireOp",EDGE,"E4");var subQ5=sQuery(id+"F0.wireOp",EDGE,"E22.filletArc");var subQ6=sQuery(id+"F0.wireOp",EDGE,"E1.bottom");var subQ7=sQuery(id+"F0.wireOp",EDGE,"E1.right");var subQ8=sQuery(id+"F0.wireOp",EDGE,"E1.top");var subQ9=sQuery(id+"F0.wireOp",EDGE,"E1.left");var subQ10=sQuery(id+"F0.wireOp",EDGE,"E23.filletArc");var subQ11=sQuery(id+"F0.wireOp",EDGE,"E24.filletArc");Q0=makeQuery(id+"F2.boolean.opBoolean","SPLIT",FACE,{"disambiguationData":[TD([makeQuery(id+"F1.opExtrude","SWEPT_FACE",FACE,{"disambiguationData":[OSD([subQ6])]})])],"derivedFrom":makeQuery(id+"F1.opExtrude","CAP_FACE",FACE,{"disambiguationData":[OSD([subQ6,subQ8,subQ9,subQ7,subQ4,subQ3,subQ2,subQ1,subQ0,subQ5,subQ10,subQ11])],"isStart":true})});}
            var sketch = newSketch(context, id + "F16", { "sketchPlane" : qUnion([Q0])});
            skLineSegment(sketch, "E79.0", {"start": v(-70, 90) * mm, "end": v(70, 90) * mm});
            skArc(sketch, "E79.1", {"start": v(-70, 90) * mm, "mid": v(-77.07, 87.07) * mm, "end": v(-80, 80) * mm});
            skLineSegment(sketch, "E79.2", {"start": v(-80, -80) * mm, "end": v(-80, 80) * mm});
            skCircle(sketch, "E79.3", {"center": v(-60, 67.5) * mm, "radius": 4 * mm});
            skArc(sketch, "E79.4", {"start": v(56.15, 48.18) * mm, "mid": v(0, 67.5) * mm, "end": v(-56.15, 48.18) * mm});
            skArc(sketch, "E79.5", {"start": v(80, 80) * mm, "mid": v(77.07, 87.07) * mm, "end": v(70, 90) * mm});
            skLineSegment(sketch, "E79.6", {"start": v(80, -80) * mm, "end": v(80, 80) * mm});
            skCircle(sketch, "E79.7", {"center": v(60, 67.5) * mm, "radius": 4 * mm});
            skArc(sketch, "E79.8", {"start": v(60, 40.3) * mm, "mid": v(58.99, 44.68) * mm, "end": v(56.15, 48.18) * mm});
            skLineSegment(sketch, "E79.9", {"start": v(60, 40.3) * mm, "end": v(60, -40.3) * mm});
            skLineSegment(sketch, "E79.10", {"start": v(-60, 40.3) * mm, "end": v(-60, -40.3) * mm});
            skArc(sketch, "E79.11", {"start": v(-56.15, 48.18) * mm, "mid": v(-58.99, 44.68) * mm, "end": v(-60, 40.3) * mm});
            skArc(sketch, "E79.12", {"start": v(-60, -40.3) * mm, "mid": v(-58.99, -44.68) * mm, "end": v(-56.15, -48.18) * mm});
            skArc(sketch, "E79.13", {"start": v(-56.15, -48.18) * mm, "mid": v(0, -67.5) * mm, "end": v(56.15, -48.18) * mm});
            skArc(sketch, "E79.14", {"start": v(56.15, -48.18) * mm, "mid": v(58.99, -44.68) * mm, "end": v(60, -40.3) * mm});
            skArc(sketch, "E79.15", {"start": v(-80, -80) * mm, "mid": v(-77.07, -87.07) * mm, "end": v(-70, -90) * mm});
            skLineSegment(sketch, "E79.16", {"start": v(-70, -90) * mm, "end": v(70, -90) * mm});
            skArc(sketch, "E79.17", {"start": v(70, -90) * mm, "mid": v(77.07, -87.07) * mm, "end": v(80, -80) * mm});
            skCircle(sketch, "E79.18", {"center": v(60, -67.5) * mm, "radius": 4 * mm});
            skCircle(sketch, "E79.19", {"center": v(-60, -67.5) * mm, "radius": 4 * mm});
            skLineSegment(sketch, "E80", {"start": v(0, 90) * mm, "end": v(0, 120) * mm});
            skLineSegment(sketch, "E81", {"start": v(-31.96, 90) * mm, "end": v(-13.96, 108) * mm});
            skLineSegment(sketch, "E82", {"start": v(0, 90) * mm, "end": v(34.04, 90) * mm});
            skLineSegment(sketch, "E83", {"start": v(34.04, 90) * mm, "end": v(16.04, 108) * mm});
            skLineSegment(sketch, "E84", {"start": v(-13.96, 108) * mm, "end": v(-13.96, 120) * mm});
            skLineSegment(sketch, "E85", {"start": v(16.04, 108) * mm, "end": v(16.04, 120) * mm});
            skArc(sketch, "E86", {"start": v(16.04, 120) * mm, "mid": v(1.04, 135) * mm, "end": v(-13.96, 120) * mm});
            skCircle(sketch, "E87", {"center": v(0, 120) * mm, "radius": 6 * mm});
            skLineSegment(sketch, "E88", {"start": v(-80, 0) * mm, "end": v(80, 0) * mm, "construction": true});
            skLineSegment(sketch, "E89.MirrorCS", {"start": v(-31.96, -90) * mm, "end": v(-13.96, -108) * mm});
            skLineSegment(sketch, "E90.MirrorCS", {"start": v(34.04, -90) * mm, "end": v(16.04, -108) * mm});
            skLineSegment(sketch, "E91.MirrorCS", {"start": v(16.04, -108) * mm, "end": v(16.04, -120) * mm});
            skArc(sketch, "E92.MirrorCS", {"start": v(16.04, -120) * mm, "mid": v(1.04, -135) * mm, "end": v(-13.96, -120) * mm});
            skLineSegment(sketch, "E93.MirrorCS", {"start": v(-13.96, -108) * mm, "end": v(-13.96, -120) * mm});
            skLineSegment(sketch, "E94.MirrorCS", {"start": v(0, -90) * mm, "end": v(0, -120) * mm});
            skCircle(sketch, "E95.MirrorC", {"center": v(0, -120) * mm, "radius": 6 * mm});
            skSolve(sketch);
        }
        {
            var Q0;
            Q0 = qSketchRegion(id + "F16", true);
            var Q1;
            Q1=makeQuery(id+"F2.opExtrude","CAP_FACE",FACE,{"disambiguationData":[OSD([sQuery(id+"F0.wireOp",EDGE,"E12"),sQuery(id+"F0.wireOp",EDGE,"E13"),sQuery(id+"F0.wireOp",EDGE,"E14"),sQuery(id+"F0.wireOp",EDGE,"E15"),sQuery(id+"F0.wireOp",EDGE,"E17.filletArc"),sQuery(id+"F0.wireOp",EDGE,"E18.filletArc"),sQuery(id+"F0.wireOp",EDGE,"E19.filletArc"),sQuery(id+"F0.wireOp",EDGE,"E20.filletArc"),sQuery(id+"F0.wireOp",EDGE,"E25.0"),sQuery(id+"F0.wireOp",EDGE,"E25.1"),sQuery(id+"F0.wireOp",EDGE,"E25.2"),sQuery(id+"F0.wireOp",EDGE,"E25.3"),sQuery(id+"F0.wireOp",EDGE,"E25.4"),sQuery(id+"F0.wireOp",EDGE,"E25.5"),sQuery(id+"F0.wireOp",EDGE,"E25.6"),sQuery(id+"F0.wireOp",EDGE,"E25.7")])],"isStart":false});
            extrude(context, id + "F17", {"entities" : qUnion([Q0]), "endBound" : BoundingType.UP_TO_SURFACE, "depth" : 25 * mm, "endBoundEntityFace" : qUnion([Q1]), "offsetDistance" : 25 * mm});
        }
    });
